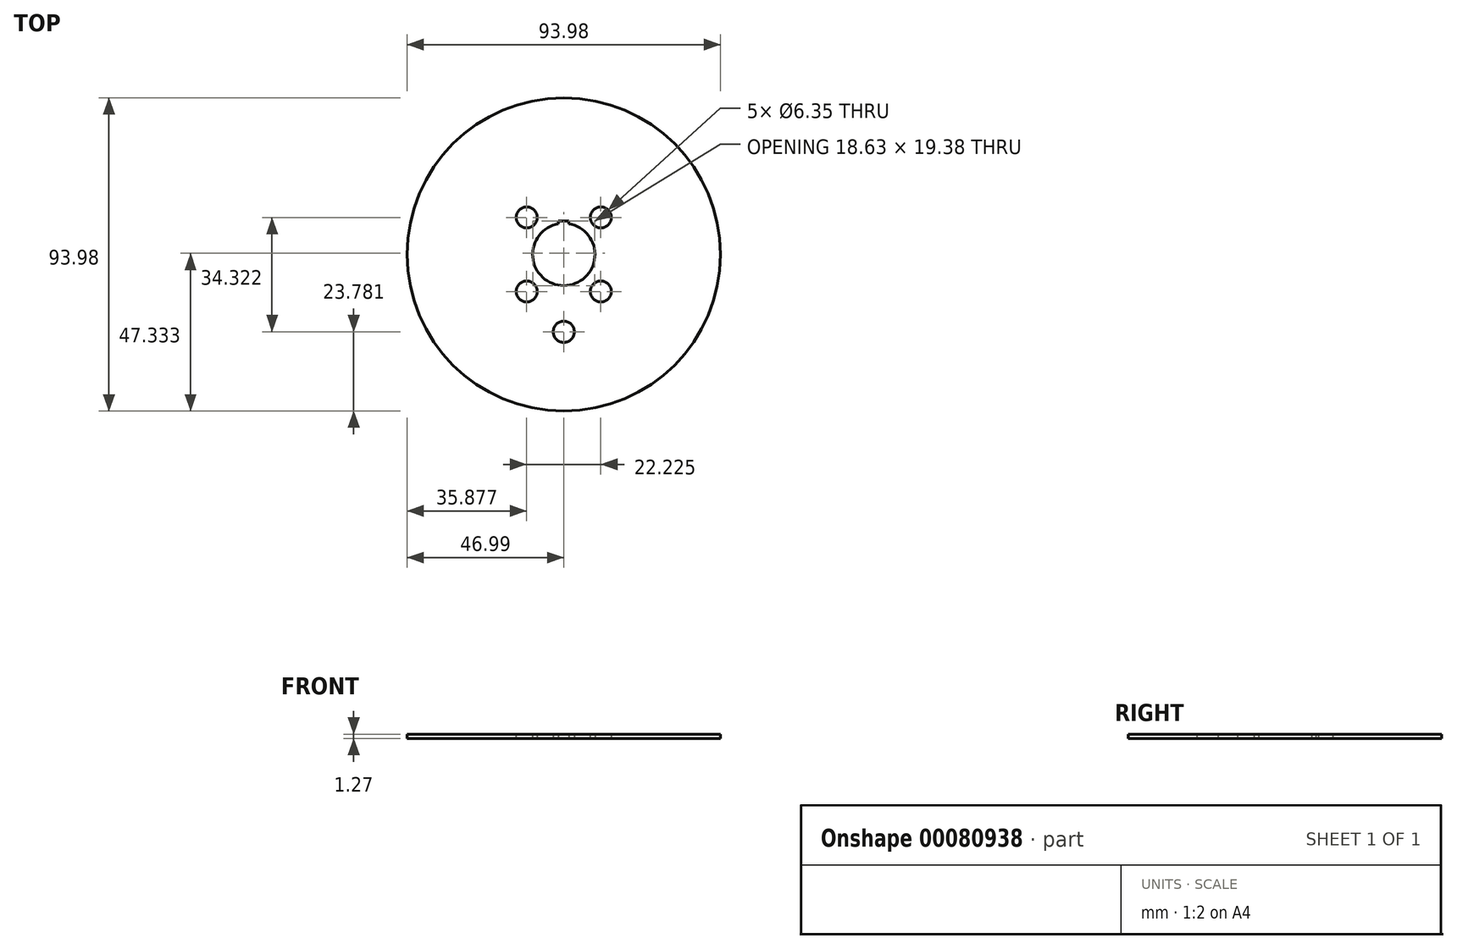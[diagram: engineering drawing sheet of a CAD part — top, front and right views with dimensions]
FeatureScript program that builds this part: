
annotation { "Feature Type Name" : "Feature", "Feature Type Description" : "" }
export const myFeature = defineFeature(function(context is Context, id is Id, definition is map)
    precondition{}
    {
        {
            var Q0;
            Q0=qCreatedBy(makeId("Top.planeOp"),FACE);
            var sketch = newSketch(context, id + "F0", { "sketchPlane" : qUnion([Q0])});
            skCircle(sketch, "E0", {"center": v(0, 0) * mm, "radius": 47 * mm});
            skCircle(sketch, "E1", {"center": v(11.11, 11.11) * mm, "radius": 3.18 * mm});
            skCircle(sketch, "E2", {"center": v(-11.11, 11.11) * mm, "radius": 3.18 * mm});
            skCircle(sketch, "E3", {"center": v(-11.11, -11.11) * mm, "radius": 3.18 * mm});
            skCircle(sketch, "E4", {"center": v(11.11, -11.11) * mm, "radius": 3.18 * mm});
            skLineSegment(sketch, "E5", {"start": v(-11.11, 11.11) * mm, "end": v(11.11, 11.11) * mm, "construction": true});
            skLineSegment(sketch, "E6", {"start": v(11.11, 11.11) * mm, "end": v(11.11, -11.11) * mm, "construction": true});
            skLineSegment(sketch, "E7", {"start": v(11.11, -11.11) * mm, "end": v(-11.11, -11.11) * mm, "construction": true});
            skLineSegment(sketch, "E8", {"start": v(-11.11, -11.11) * mm, "end": v(-11.11, 11.11) * mm, "construction": true});
            skCircle(sketch, "E9", {"center": v(0, 0) * mm, "radius": 9.35 * mm});
            skCircle(sketch, "E10", {"center": v(0, -23.2) * mm, "radius": 3.18 * mm});
            skLineSegment(sketch, "E11.bottom", {"start": v(-1.59, 0) * mm, "end": v(1.59, 0) * mm});
            skLineSegment(sketch, "E11.top", {"start": v(-1.59, 10.03) * mm, "end": v(1.59, 10.03) * mm});
            skLineSegment(sketch, "E11.left", {"start": v(-1.59, 0) * mm, "end": v(-1.59, 10.03) * mm});
            skLineSegment(sketch, "E11.right", {"start": v(1.59, 0) * mm, "end": v(1.59, 10.03) * mm});
            skSolve(sketch);
        }
        {
            var Q0;
            Q0=makeQuery(id+"F0.imprint","IMPRINT",FACE,{"disambiguationData":[TD([[makeQuery(id+"F0.imprint","IMPRINT",EDGE,{"derivedFrom":sQuery(id+"F0.wireOp",EDGE,"E0")}),1.0]])]});
            extrude(context, id + "F1", {"entities" : qUnion([Q0]), "depth" : 1.27 * mm});
        }
    });
